# Revit family: Gira_236500
name_source: partatom
category: Electrical Fixtures
revit_build: Autodesk Revit 2017 (Build: 20160225_1515(x64)
units: mm (PartAtom-declared; Revit-internal decimal feet)

## family parameters
Cut with Voids When Loaded = No
Host = Face
Maintain Annotation Orientation = No
Part Type = Normal
Room Calculation Point = No
Round Connector Dimension = Use Diameter
Shared = No

## types (1)
- S3000 uni.LED dim. DRA Electronics
    Anschlussart = Screwed terminal
    App control via Bluetooth = No
    Applicable with button = Yes
    Applicable with infrared button = No
    Applicable with movement sensor = Yes
    Applicable with presence indicator = Yes
    Applicable with time switch/timer = No
    Applicable with transmission button = No
    BIM = https://media.live.bim.site X1 REG KNX.rfa
    BIMSITE_PRODUCT_ID = 8f91fb907f181f1ec18f10e8b15fd6913afbe936
    Bus connection included = No
    Cost = 0 $
    Default Elevation = 1219 mm
    Description = S3000 uni.LED dim.DRA Elec. System 3000 universal LED dimmer DRA,DRA Features: - Switching and dimming light bulbs, HV halogen lamps, electronic transformers for halogen or LED lamps, dimmable inductive transformers for halogen or LED lamps, HV LED or compact fluorescent lamps. - Switching and dimming light bulbs, HV halogen lamps, electronic transformers for halogen or LED lamps, dimmable inductive transformers for halogen or LED lamps, HV LED or compact fluorescent lamps. - Operation is via mechanical button (NO contact), System 3000 2- or 3-wire auxiliary unit or System 2000 2-wire auxiliary unit. - Automatic or manual setting of dimming principle according to load (leading or trailing edge). - Display of the selected operating mode using LED. - Bulb-saving switch-on. - Switch-on brightness can be saved permanently (possible with System 2000 and 3000 auxiliary unit). - Switch on with the last brightness set, or a saved switch-on brightness. - Minimum brightness can be set. - Electronic short-circuit protection. - Electronic excess-temperature protection. - Operation with neutral conductor connection.,Notes : - If the ambient temperature is higher than 45 C, the connected load must be reduced.
    Dimming phase cut-off = No
    Dimming phase cut-on = No
    Frequency [Hz] = [50:60]
    GTIN = 4010337031376
    HAN = 236500
    Halogen free = No
    HeinzeBIM = https://www.heinze.de
    Light value memory = No
    Manufacturer = Gira
    Material = Sonstige (*de-DE)
    Material quality = Sonstige (*de-DE)
    Method of operation = Sonstige (*de-DE)
    Nominal voltage [Volt] = [230:230]
    Number of inputs = 0
    Radio frequent bidirectional = No
    Serial dimmer = No
    Suitable for degree of protection (IP) = IP20
    Surface protection = Sonstige (*de-DE)
    Transparent = No
    Type of fastening = Snapper mounting
    Type of load = Universal and LED Retrofit
    URL = https://www.gira.de
    With label area = No
    Zusammenstellung = Basic element with complete housing

## geometry (parser evidence)
native form markers: Blend x2, Sweep x3
no freeform markers — native parametric forms only
